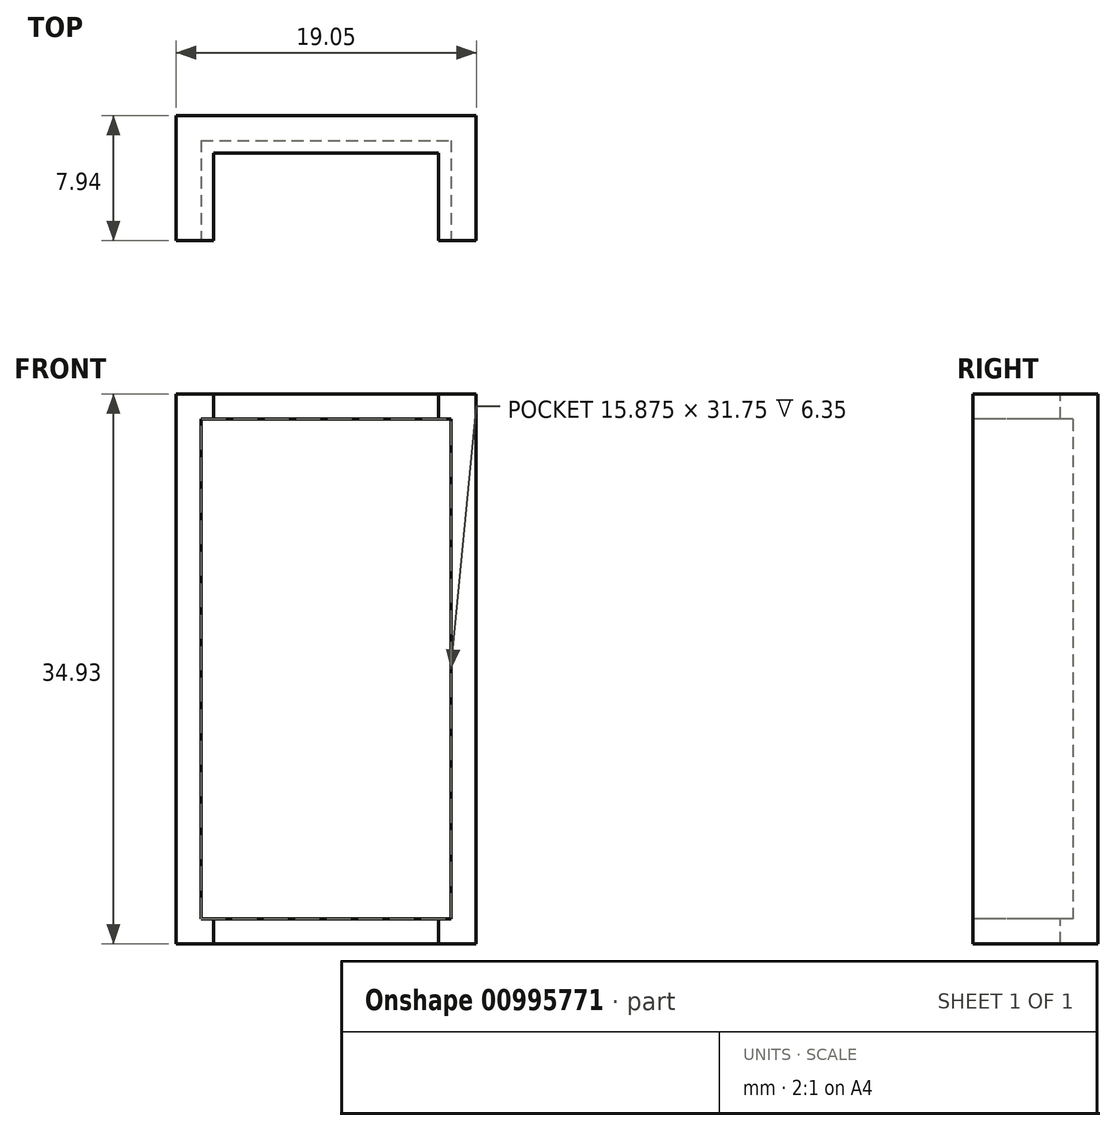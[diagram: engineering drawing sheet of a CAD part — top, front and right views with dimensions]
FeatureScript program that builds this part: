
annotation { "Feature Type Name" : "Feature", "Feature Type Description" : "" }
export const myFeature = defineFeature(function(context is Context, id is Id, definition is map)
    precondition{}
    {
        {
            var Q0;
            Q0=qCreatedBy(makeId("Front.planeOp"),FACE);
            var sketch = newSketch(context, id + "F0", { "sketchPlane" : qUnion([Q0])});
            skLineSegment(sketch, "E0.bottom", {"start": v(-44.56, 46.1) * mm, "end": v(-25.51, 46.1) * mm});
            skLineSegment(sketch, "E0.top", {"start": v(-44.56, 11.17) * mm, "end": v(-25.51, 11.17) * mm});
            skLineSegment(sketch, "E0.left", {"start": v(-44.56, 46.1) * mm, "end": v(-44.56, 11.17) * mm});
            skLineSegment(sketch, "E0.right", {"start": v(-25.51, 46.1) * mm, "end": v(-25.51, 11.17) * mm});
            skSolve(sketch);
        }
        {
            var Q0;
            Q0=makeQuery(id+"F0.imprint","IMPRINT",FACE,{"disambiguationData":[TD([[makeQuery(id+"F0.imprint","IMPRINT",EDGE,{"derivedFrom":sQuery(id+"F0.wireOp",EDGE,"E0.bottom")}),-1.0]])]});
            extrude(context, id + "F1", {"entities" : qUnion([Q0]), "depth" : 7.94 * mm, "offsetDistance" : 25.4 * mm});
        }
        {
            var Q0;
            Q0=makeQuery(id+"F1.opExtrude","CAP_FACE",FACE,{"disambiguationData":[OSD([sQuery(id+"F0.wireOp",EDGE,"E0.bottom"),sQuery(id+"F0.wireOp",EDGE,"E0.top"),sQuery(id+"F0.wireOp",EDGE,"E0.left"),sQuery(id+"F0.wireOp",EDGE,"E0.right")])],"isStart":false});
            var sketch = newSketch(context, id + "F2", { "sketchPlane" : qUnion([Q0])});
            skLineSegment(sketch, "E1.0", {"start": v(-42.98, 44.51) * mm, "end": v(-42.98, 12.76) * mm});
            skLineSegment(sketch, "E2.0", {"start": v(-42.98, 12.76) * mm, "end": v(-27.1, 12.76) * mm});
            skLineSegment(sketch, "E3.0", {"start": v(-27.1, 44.51) * mm, "end": v(-27.1, 12.76) * mm});
            skLineSegment(sketch, "E4.0", {"start": v(-42.98, 44.51) * mm, "end": v(-27.1, 44.51) * mm});
            skSolve(sketch);
        }
        {
            var Q0;
            Q0=makeQuery(id+"F2.imprint","IMPRINT",FACE,{"disambiguationData":[TD([[makeQuery(id+"F2.imprint","IMPRINT",EDGE,{"derivedFrom":sQuery(id+"F2.wireOp",EDGE,"E1.0")}),1.0]])]});
            extrude(context, id + "F3", {"entities" : qUnion([Q0]), "operationType" : NewBodyOperationType.REMOVE, "oppositeDirection" : true, "depth" : 6.35 * mm, "offsetDistance" : 25.4 * mm});
        }
        {
            var Q0;
            Q0=makeQuery(id+"F1.opExtrude","SWEPT_FACE",FACE,{"disambiguationData":[OSD([sQuery(id+"F0.wireOp",EDGE,"E0.bottom")])]});
            var sketch = newSketch(context, id + "F4", { "sketchPlane" : qUnion([Q0])});
            skLineSegment(sketch, "E5", {"start": v(-42.18, -7.94) * mm, "end": v(-42.18, -2.38) * mm});
            skLineSegment(sketch, "E6", {"start": v(-42.18, -2.38) * mm, "end": v(-27.9, -2.38) * mm});
            skLineSegment(sketch, "E7", {"start": v(-27.9, -2.38) * mm, "end": v(-27.9, -7.94) * mm});
            skSolve(sketch);
        }
        {
            var Q0;
            {var subQ0=sQuery(id+"F4.wireOp",EDGE,"E5");Q0=makeQuery(id+"F4.imprint","IMPRINT",FACE,{"disambiguationData":[TD([[makeQuery(id+"F4.imprint","IMPRINT",EDGE,{"derivedFrom":subQ0}),-1.0]])]});}
            extrude(context, id + "F5", {"entities" : qUnion([Q0]), "operationType" : NewBodyOperationType.REMOVE, "endBound" : BoundingType.THROUGH_ALL, "oppositeDirection" : true, "depth" : 25.4 * mm, "offsetDistance" : 25.4 * mm});
        }
    });
